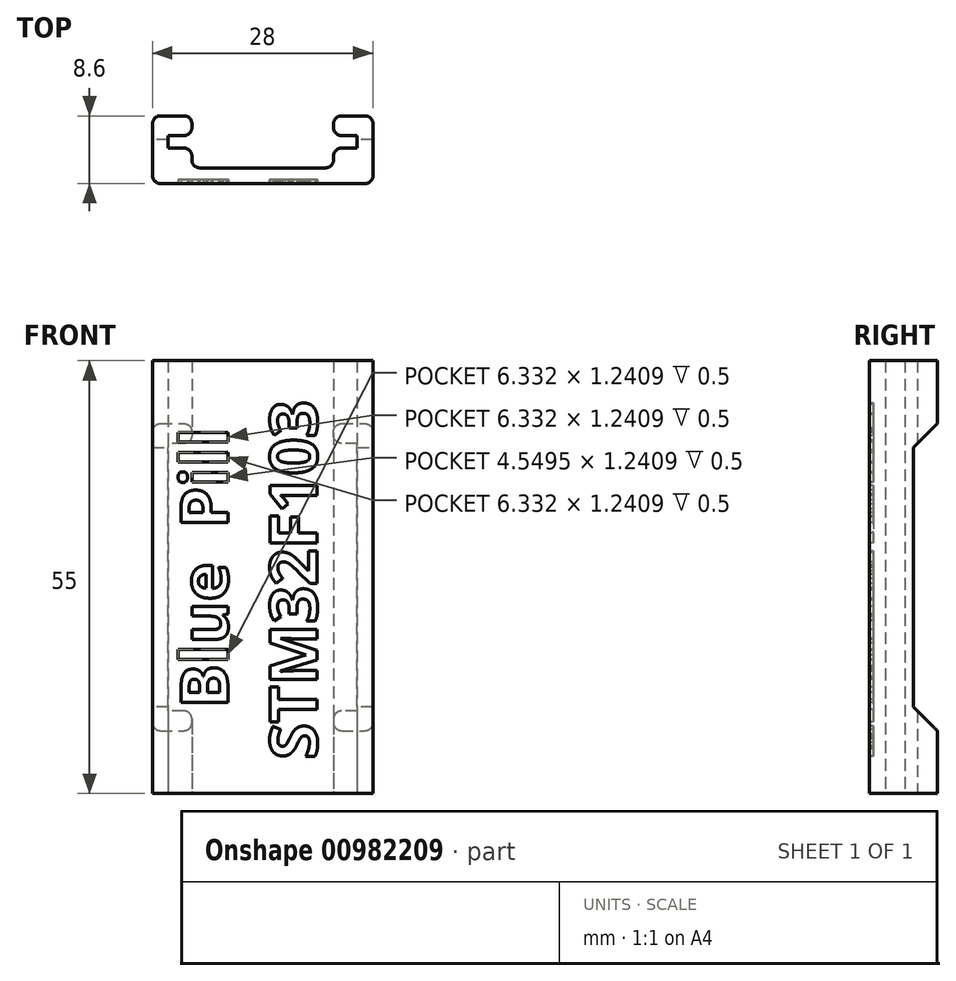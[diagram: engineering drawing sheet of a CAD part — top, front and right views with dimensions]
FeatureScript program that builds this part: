
annotation { "Feature Type Name" : "Feature", "Feature Type Description" : "" }
export const myFeature = defineFeature(function(context is Context, id is Id, definition is map)
    precondition{}
    {
        {
            var Q0;
            Q0=qCreatedBy(makeId("Top.planeOp"),FACE);
            var sketch = newSketch(context, id + "F0", { "sketchPlane" : qUnion([Q0])});
            skLineSegment(sketch, "E0", {"start": v(1, 0) * mm, "end": v(14, 0) * mm});
            skLineSegment(sketch, "E1", {"start": v(14, 10.75) * mm, "end": v(14, -18.5) * mm, "construction": true});
            skLineSegment(sketch, "E2", {"start": v(0, 1) * mm, "end": v(0, 7.6) * mm});
            skLineSegment(sketch, "E3", {"start": v(1, 8.6) * mm, "end": v(4, 8.6) * mm});
            skLineSegment(sketch, "E4", {"start": v(5, 7.6) * mm, "end": v(5, 7.1) * mm});
            skLineSegment(sketch, "E5", {"start": v(4, 6.1) * mm, "end": v(2, 6.1) * mm});
            skLineSegment(sketch, "E6", {"start": v(2, 6.1) * mm, "end": v(2, 4.5) * mm});
            skLineSegment(sketch, "E7", {"start": v(2, 4.5) * mm, "end": v(4, 4.5) * mm});
            skLineSegment(sketch, "E8", {"start": v(5, 3.5) * mm, "end": v(5, 3) * mm});
            skLineSegment(sketch, "E9", {"start": v(6, 2) * mm, "end": v(14, 2) * mm});
            skPoint(sketch, "E10.visualSharp", {"position": v(5, 2) * mm});
            skArc(sketch, "E10.filletArc", {"start": v(5, 3) * mm, "mid": v(5.3, 2.3) * mm, "end": v(6, 2) * mm});
            skPoint(sketch, "E11.visualSharp", {"position": v(5, 4.5) * mm});
            skArc(sketch, "E11.filletArc", {"start": v(5, 3.5) * mm, "mid": v(4.7, 4.2) * mm, "end": v(4, 4.5) * mm});
            skPoint(sketch, "E12.visualSharp", {"position": v(5, 6.1) * mm});
            skArc(sketch, "E12.filletArc", {"start": v(4, 6.1) * mm, "mid": v(4.7, 6.4) * mm, "end": v(5, 7.1) * mm});
            skPoint(sketch, "E13.visualSharp", {"position": v(5, 8.6) * mm});
            skArc(sketch, "E13.filletArc", {"start": v(5, 7.6) * mm, "mid": v(4.7, 8.3) * mm, "end": v(4, 8.6) * mm});
            skPoint(sketch, "E14.visualSharp", {"position": v(0, 8.6) * mm});
            skArc(sketch, "E14.filletArc", {"start": v(1, 8.6) * mm, "mid": v(0.3, 8.3) * mm, "end": v(0, 7.6) * mm});
            skPoint(sketch, "E15.visualSharp", {"position": v(0, 0) * mm});
            skArc(sketch, "E15.filletArc", {"start": v(0, 1) * mm, "mid": v(0.3, 0.3) * mm, "end": v(1, 0) * mm});
            skArc(sketch, "E16.MirrorCS", {"start": v(23, 3) * mm, "mid": v(22.7, 2.3) * mm, "end": v(22, 2) * mm});
            skLineSegment(sketch, "E17.MirrorCS", {"start": v(22, 2) * mm, "end": v(14, 2) * mm});
            skLineSegment(sketch, "E18.MirrorCS", {"start": v(24, 6.1) * mm, "end": v(26, 6.1) * mm});
            skPoint(sketch, "E19.MirrorP", {"position": v(28, 0) * mm});
            skArc(sketch, "E20.MirrorCS", {"start": v(28, 1) * mm, "mid": v(27.7, 0.3) * mm, "end": v(27, 0) * mm});
            skPoint(sketch, "E21.MirrorP", {"position": v(23, 8.6) * mm});
            skArc(sketch, "E22.MirrorCS", {"start": v(27, 8.6) * mm, "mid": v(27.7, 8.3) * mm, "end": v(28, 7.6) * mm});
            skLineSegment(sketch, "E23.MirrorCS", {"start": v(27, 8.6) * mm, "end": v(24, 8.6) * mm});
            skPoint(sketch, "E24.MirrorP", {"position": v(23, 6.1) * mm});
            skPoint(sketch, "E25.MirrorP", {"position": v(28, 8.6) * mm});
            skLineSegment(sketch, "E26.MirrorCS", {"start": v(27, 0) * mm, "end": v(14, 0) * mm});
            skLineSegment(sketch, "E27.MirrorCS", {"start": v(28, 1) * mm, "end": v(28, 7.6) * mm});
            skArc(sketch, "E28.MirrorCS", {"start": v(24, 6.1) * mm, "mid": v(23.3, 6.4) * mm, "end": v(23, 7.1) * mm});
            skArc(sketch, "E29.MirrorCS", {"start": v(23, 7.6) * mm, "mid": v(23.3, 8.3) * mm, "end": v(24, 8.6) * mm});
            skLineSegment(sketch, "E30.MirrorCS", {"start": v(26, 4.5) * mm, "end": v(24, 4.5) * mm});
            skLineSegment(sketch, "E31.MirrorCS", {"start": v(23, 3.5) * mm, "end": v(23, 3) * mm});
            skLineSegment(sketch, "E32.MirrorCS", {"start": v(26, 6.1) * mm, "end": v(26, 4.5) * mm});
            skLineSegment(sketch, "E33.MirrorCS", {"start": v(23, 7.6) * mm, "end": v(23, 7.1) * mm});
            skPoint(sketch, "E34.MirrorP", {"position": v(23, 2) * mm});
            skArc(sketch, "E35.MirrorCS", {"start": v(23, 3.5) * mm, "mid": v(23.3, 4.2) * mm, "end": v(24, 4.5) * mm});
            skPoint(sketch, "E36.MirrorP", {"position": v(23, 4.5) * mm});
            skSolve(sketch);
        }
        {
            var Q0;
            Q0 = qSketchRegion(id + "F0", true);
            extrude(context, id + "F1", {"entities" : qUnion([Q0]), "depth" : 55 * mm, "offsetDistance" : 25 * mm});
        }
        {
            var Q0;
            Q0=makeQuery(id+"F1.opExtrude","SWEPT_FACE",FACE,{"disambiguationData":[OSD([sQuery(id+"F0.wireOp",EDGE,"E0"),sQuery(id+"F0.wireOp",EDGE,"E26.MirrorCS")])]});
            var sketch = newSketch(context, id + "F2", { "sketchPlane" : qUnion([Q0])});
            skText(sketch, "E37", { "text": "   Blue  Pill\nSTM32F103", "fontName": "OpenSans-Bold.ttf"});
            const initialGuessF2  = {"E37": [0.00957, 0.00433, 0, 1, 0.006]};
            skSetInitialGuess(sketch, initialGuessF2);
            skSolve(sketch);
        }
        {
            var Q0;
            Q0 = qSketchRegion(id + "F2", true);
            extrude(context, id + "F3", {"entities" : qUnion([Q0]), "operationType" : NewBodyOperationType.REMOVE, "oppositeDirection" : true, "depth" : 0.5 * mm, "offsetDistance" : 25 * mm});
        }
        {
            var Q0;
            Q0=makeQuery(id+"F1.opExtrude","SWEPT_FACE",FACE,{"disambiguationData":[OSD([sQuery(id+"F0.wireOp",EDGE,"E23.MirrorCS")])]});
            var sketch = newSketch(context, id + "F4", { "sketchPlane" : qUnion([Q0])});
            skLineSegment(sketch, "E38.bottom", {"start": v(-31.8, 50) * mm, "end": v(6.26, 50) * mm});
            skLineSegment(sketch, "E38.top", {"start": v(-31.8, 5) * mm, "end": v(6.26, 5) * mm});
            skLineSegment(sketch, "E38.left", {"start": v(-31.8, 50) * mm, "end": v(-31.8, 5) * mm});
            skLineSegment(sketch, "E38.right", {"start": v(6.26, 50) * mm, "end": v(6.26, 5) * mm});
            skSolve(sketch);
        }
        {
            var Q0;
            Q0 = qSketchRegion(id + "F4", true);
            var Q1;
            Q1=makeQuery(id+"F1.opExtrude","SWEPT_FACE",FACE,{"disambiguationData":[OSD([sQuery(id+"F0.wireOp",EDGE,"E30.MirrorCS")])]});
            extrude(context, id + "F5", {"entities" : qUnion([Q0]), "operationType" : NewBodyOperationType.REMOVE, "oppositeDirection" : true, "depth" : 3 * mm, "endBoundEntityFace" : qUnion([Q1]), "offsetDistance" : 25 * mm});
        }
        {
            var Q0;
            {var subQ0=sQuery(id+"F4.wireOp",EDGE,"E38.bottom");Q0=makeQuery(id+"F5.boolean.opBoolean","COPY",EDGE,{"disambiguationData":[topologyDisambiguationEdgeConnected([makeQuery(id+"F1.opExtrude","SWEPT_FACE",FACE,{"disambiguationData":[OSD([sQuery(id+"F0.wireOp",EDGE,"E7")])]})])],"derivedFrom":makeQuery(id+"F5.opExtrude","CAP_EDGE",EDGE,{"disambiguationData":[OSD([subQ0])],"isStart":false})});}
            var Q1;
            {var subQ0=sQuery(id+"F4.wireOp",EDGE,"E38.bottom");Q1=makeQuery(id+"F5.boolean.opBoolean","COPY",EDGE,{"disambiguationData":[topologyDisambiguationEdgeConnected([makeQuery(id+"F1.opExtrude","SWEPT_FACE",FACE,{"disambiguationData":[OSD([sQuery(id+"F0.wireOp",EDGE,"E30.MirrorCS")])]})])],"derivedFrom":makeQuery(id+"F5.opExtrude","CAP_EDGE",EDGE,{"disambiguationData":[OSD([subQ0])],"isStart":false})});}
            var Q2;
            {var subQ0=sQuery(id+"F4.wireOp",EDGE,"E38.top");Q2=makeQuery(id+"F5.boolean.opBoolean","COPY",EDGE,{"disambiguationData":[topologyDisambiguationEdgeConnected([makeQuery(id+"F1.opExtrude","SWEPT_FACE",FACE,{"disambiguationData":[OSD([sQuery(id+"F0.wireOp",EDGE,"E7")])]})])],"derivedFrom":makeQuery(id+"F5.opExtrude","CAP_EDGE",EDGE,{"disambiguationData":[OSD([subQ0])],"isStart":false})});}
            var Q3;
            {var subQ0=sQuery(id+"F4.wireOp",EDGE,"E38.top");Q3=makeQuery(id+"F5.boolean.opBoolean","COPY",EDGE,{"disambiguationData":[topologyDisambiguationEdgeConnected([makeQuery(id+"F1.opExtrude","SWEPT_FACE",FACE,{"disambiguationData":[OSD([sQuery(id+"F0.wireOp",EDGE,"E30.MirrorCS")])]})])],"derivedFrom":makeQuery(id+"F5.opExtrude","CAP_EDGE",EDGE,{"disambiguationData":[OSD([subQ0])],"isStart":false})});}
            chamfer(context, id + "F6", {"entities" : qUnion([Q0, Q1, Q2, Q3]), "chamferType" : ChamferType.OFFSET_ANGLE, "width" : 6 * mm, "oppositeDirection" : false, "angle" : 45 * degree, "tangentPropagation" : true});
        }
    });
